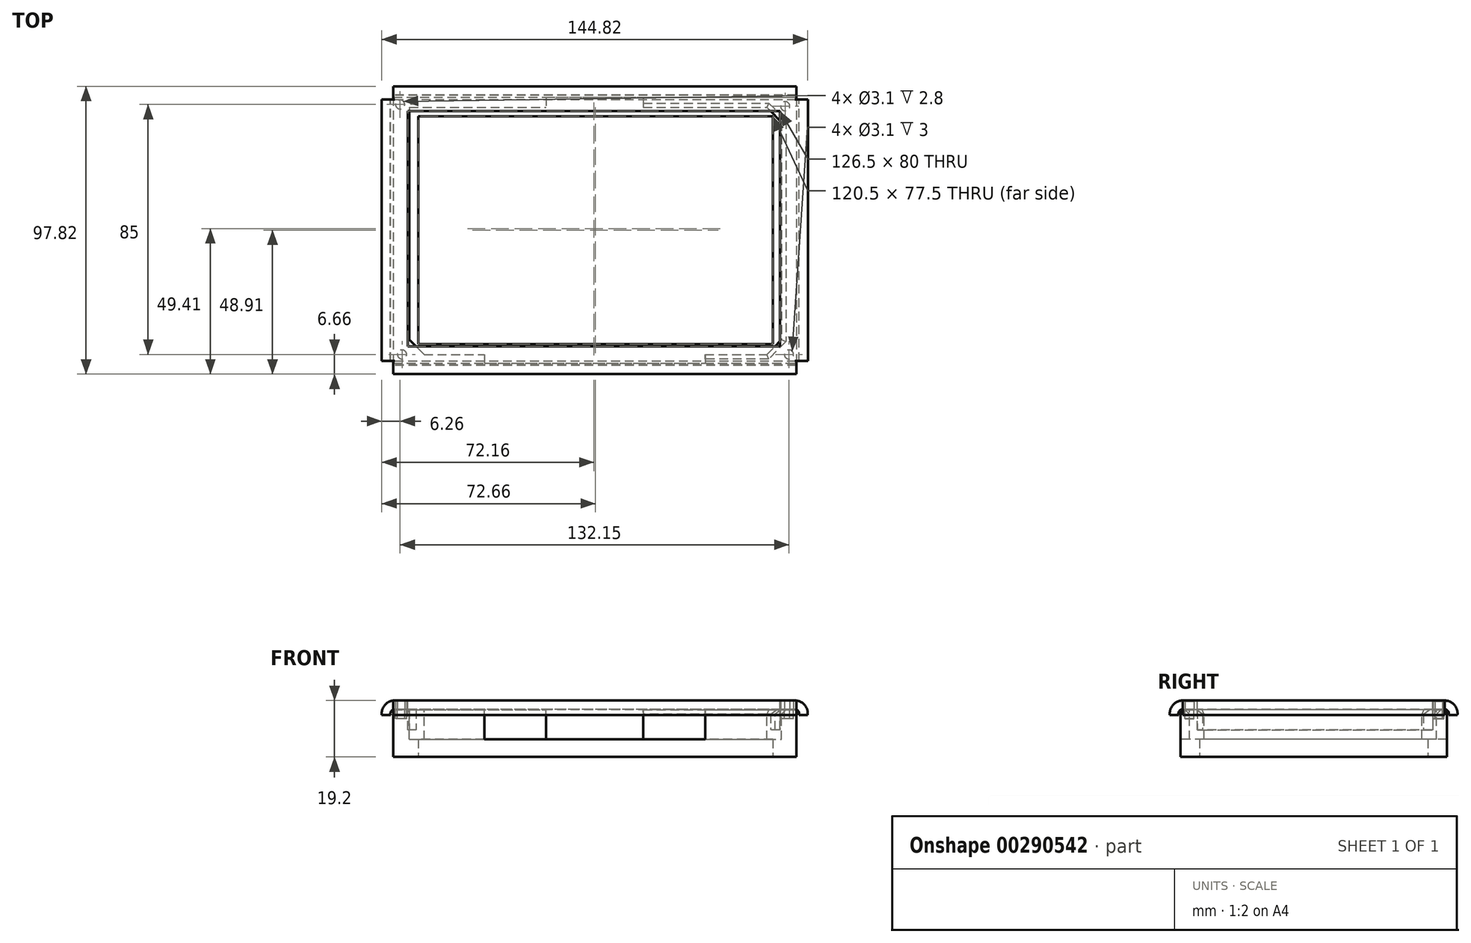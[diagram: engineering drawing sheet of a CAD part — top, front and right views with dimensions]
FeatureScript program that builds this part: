
annotation { "Feature Type Name" : "Feature", "Feature Type Description" : "" }
export const myFeature = defineFeature(function(context is Context, id is Id, definition is map)
    precondition{}
    {
        {
            var Q0;
            Q0=qCreatedBy(makeId("Top.planeOp"),FACE);
            var sketch = newSketch(context, id + "F0", { "sketchPlane" : qUnion([Q0])});
            skLineSegment(sketch, "E0.top", {"start": v(-68.5, -45.25) * mm, "end": v(68.5, -45.25) * mm});
            skLineSegment(sketch, "E0.left", {"start": v(-68.5, 45.25) * mm, "end": v(-68.5, -45.25) * mm});
            skLineSegment(sketch, "E0.right", {"start": v(68.5, 45.25) * mm, "end": v(68.5, -45.25) * mm});
            skLineSegment(sketch, "E1.top", {"start": v(-60, -38.75) * mm, "end": v(60.5, -38.75) * mm});
            skLineSegment(sketch, "E1.left", {"start": v(-60, 38.75) * mm, "end": v(-60, -38.75) * mm});
            skLineSegment(sketch, "E1.right", {"start": v(60.5, 38.75) * mm, "end": v(60.5, -38.75) * mm});
            skLineSegment(sketch, "E2", {"start": v(-68.5, 45.25) * mm, "end": v(68.5, 45.25) * mm});
            skLineSegment(sketch, "E3", {"start": v(60.5, 38.75) * mm, "end": v(-60, 38.75) * mm});
            skSolve(sketch);
        }
        {
            var Q0;
            Q0=makeQuery(id+"F0.imprint","IMPRINT",FACE,{"disambiguationData":[TD([[makeQuery(id+"F0.imprint","IMPRINT",EDGE,{"derivedFrom":sQuery(id+"F0.wireOp",EDGE,"E0.top")}),1.0]])]});
            extrude(context, id + "F1", {"entities" : qUnion([Q0]), "depth" : 16 * mm});
        }
        {
            var Q0;
            Q0=makeQuery(id+"F1.opExtrude","CAP_VERTEX",VERTEX,{"disambiguationData":[OSD([sQuery(id+"F0.wireOp",EDGE,"E0.left"),sQuery(id+"F0.wireOp",EDGE,"E2")])],"isStart":false});
            var Q1;
            Q1=makeQuery(id+"F1.opExtrude","CAP_VERTEX",VERTEX,{"disambiguationData":[OSD([sQuery(id+"F0.wireOp",EDGE,"E1.left"),sQuery(id+"F0.wireOp",EDGE,"E3")])],"isStart":false});
            var Q2;
            Q2=makeQuery(id+"F1.opExtrude","CAP_VERTEX",VERTEX,{"disambiguationData":[OSD([sQuery(id+"F0.wireOp",EDGE,"E1.top"),sQuery(id+"F0.wireOp",EDGE,"E1.left")])],"isStart":false});
            cPlane(context, id + "F2", {"entities" : qUnion([Q0, Q1, Q2]), "cplaneType" : CPlaneType.THREE_POINT, "offset" : 25 * mm, "width" : 150 * mm, "height" : 150 * mm});
        }
        {
            var Q0;
            Q0=qCreatedBy(id+"F2.planeOp",FACE);
            var sketch = newSketch(context, id + "F3", { "sketchPlane" : qUnion([Q0])});
            skLineSegment(sketch, "E4.bottom", {"start": v(-16.5, 80.88) * mm, "end": v(16.5, 80.88) * mm});
            skLineSegment(sketch, "E4.top", {"start": v(-16.5, 28.75) * mm, "end": v(16.5, 28.75) * mm});
            skLineSegment(sketch, "E4.left", {"start": v(-16.5, 80.88) * mm, "end": v(-16.5, 28.75) * mm});
            skLineSegment(sketch, "E4.right", {"start": v(16.5, 80.88) * mm, "end": v(16.5, 28.75) * mm});
            skLineSegment(sketch, "E5.bottom", {"start": v(-63, 41.75) * mm, "end": v(58.5, 41.75) * mm});
            skLineSegment(sketch, "E5.top", {"start": v(-58, -42.25) * mm, "end": v(58.5, -42.25) * mm});
            skLineSegment(sketch, "E5.left", {"start": v(-63, 41.75) * mm, "end": v(-63, -37.25) * mm});
            skLineSegment(sketch, "E6.bottom", {"start": v(37.5, -28.75) * mm, "end": v(-37.5, -28.75) * mm});
            skLineSegment(sketch, "E6.top", {"start": v(37.5, -48.75) * mm, "end": v(-37.5, -48.75) * mm});
            skLineSegment(sketch, "E6.left", {"start": v(37.5, -28.75) * mm, "end": v(37.5, -48.75) * mm});
            skLineSegment(sketch, "E6.right", {"start": v(-37.5, -28.75) * mm, "end": v(-37.5, -48.75) * mm});
            skLineSegment(sketch, "E7", {"start": v(-63, -37.25) * mm, "end": v(-58, -42.25) * mm});
            skLineSegment(sketch, "E8", {"start": v(58.5, -42.25) * mm, "end": v(63.5, -37.25) * mm});
            skLineSegment(sketch, "E9", {"start": v(58.5, 41.75) * mm, "end": v(63.5, 36.75) * mm});
            skLineSegment(sketch, "E10", {"start": v(63.5, 36.75) * mm, "end": v(63.5, -37.25) * mm});
            skSolve(sketch);
        }
        {
            var Q0;
            {var subQ0=sQuery(id+"F3.wireOp",EDGE,"E4.bottom");Q0=makeQuery(id+"F3.imprint","IMPRINT",FACE,{"disambiguationData":[TD([[makeQuery(id+"F3.imprint","IMPRINT",EDGE,{"derivedFrom":subQ0}),-1.0]])]});}
            var Q1;
            {var subQ0=sQuery(id+"F3.wireOp",EDGE,"E4.top");Q1=makeQuery(id+"F3.imprint","IMPRINT",FACE,{"disambiguationData":[TD([[makeQuery(id+"F3.imprint","IMPRINT",EDGE,{"derivedFrom":subQ0}),1.0]])]});}
            var Q2;
            {var subQ10=sQuery(id+"F3.wireOp",EDGE,"E4.top");Q2=makeQuery(id+"F3.imprint","IMPRINT",FACE,{"disambiguationData":[TD([[makeQuery(id+"F3.imprint","IMPRINT",EDGE,{"derivedFrom":subQ10}),-1.0]])]});}
            var Q3;
            {var subQ5=sQuery(id+"F3.wireOp",EDGE,"E6.bottom");Q3=makeQuery(id+"F3.imprint","IMPRINT",FACE,{"disambiguationData":[TD([[makeQuery(id+"F3.imprint","IMPRINT",EDGE,{"derivedFrom":subQ5}),1.0]])]});}
            var Q4;
            {var subQ5=sQuery(id+"F3.wireOp",EDGE,"E6.top");Q4=makeQuery(id+"F3.imprint","IMPRINT",FACE,{"disambiguationData":[TD([[makeQuery(id+"F3.imprint","IMPRINT",EDGE,{"derivedFrom":subQ5}),-1.0]])]});}
            extrude(context, id + "F4", {"entities" : qUnion([Q0, Q1, Q2, Q3, Q4]), "operationType" : NewBodyOperationType.REMOVE, "oppositeDirection" : true, "depth" : 10 * mm});
        }
        {
            var Q0;
            Q0=makeQuery(id+"F4.boolean.opBoolean","COPY",EDGE,{"derivedFrom":makeQuery(id+"F4.opExtrude","CAP_EDGE",EDGE,{"disambiguationData":[OSD([sQuery(id+"F3.wireOp",EDGE,"E5.left")])],"isStart":true})});
            var Q1;
            {var subQ0=sQuery(id+"F3.wireOp",EDGE,"E5.bottom");Q1=makeQuery(id+"F4.boolean.opBoolean","COPY",EDGE,{"derivedFrom":makeQuery(id+"F4.opExtrude","CAP_EDGE",EDGE,{"disambiguationData":[OSD([subQ0]),TDD([makeQuery(id+"F3.imprint","IMPRINT",EDGE,{"disambiguationData":[TD([[makeQuery(id+"F3.imprint","INTERSECT",VERTEX,{"derivedFrom":[subQ0,sQuery(id+"F3.wireOp",EDGE,"E5.left")]}),-1.0]])],"derivedFrom":subQ0})])],"isStart":true})});}
            var Q2;
            {var subQ0=sQuery(id+"F3.wireOp",EDGE,"E5.bottom");Q2=makeQuery(id+"F4.boolean.opBoolean","COPY",EDGE,{"derivedFrom":makeQuery(id+"F4.opExtrude","CAP_EDGE",EDGE,{"disambiguationData":[OSD([subQ0]),TDD([makeQuery(id+"F3.imprint","IMPRINT",EDGE,{"disambiguationData":[TD([[makeQuery(id+"F3.imprint","INTERSECT",VERTEX,{"derivedFrom":[subQ0,sQuery(id+"F3.wireOp",EDGE,"E5.right")]}),1.0]])],"derivedFrom":subQ0})])],"isStart":true})});}
            var Q3;
            Q3=makeQuery(id+"F4.boolean.opBoolean","COPY",EDGE,{"derivedFrom":makeQuery(id+"F4.opExtrude","CAP_EDGE",EDGE,{"disambiguationData":[OSD([sQuery(id+"F3.wireOp",EDGE,"E5.right")])],"isStart":true})});
            var Q4;
            {var subQ0=sQuery(id+"F3.wireOp",EDGE,"E5.top");Q4=makeQuery(id+"F4.boolean.opBoolean","COPY",EDGE,{"derivedFrom":makeQuery(id+"F4.opExtrude","CAP_EDGE",EDGE,{"disambiguationData":[OSD([subQ0]),TDD([makeQuery(id+"F3.imprint","IMPRINT",EDGE,{"disambiguationData":[TD([[makeQuery(id+"F3.imprint","INTERSECT",VERTEX,{"derivedFrom":[subQ0,sQuery(id+"F3.wireOp",EDGE,"E5.right")]}),1.0]])],"derivedFrom":subQ0})])],"isStart":true})});}
            var Q5;
            {var subQ0=sQuery(id+"F3.wireOp",EDGE,"E5.top");Q5=makeQuery(id+"F4.boolean.opBoolean","COPY",EDGE,{"derivedFrom":makeQuery(id+"F4.opExtrude","CAP_EDGE",EDGE,{"disambiguationData":[OSD([subQ0]),TDD([makeQuery(id+"F3.imprint","IMPRINT",EDGE,{"disambiguationData":[TD([[makeQuery(id+"F3.imprint","INTERSECT",VERTEX,{"derivedFrom":[subQ0,sQuery(id+"F3.wireOp",EDGE,"E5.left")]}),-1.0]])],"derivedFrom":subQ0})])],"isStart":true})});}
            var Q6;
            Q6=makeQuery(id+"F4.boolean.opBoolean","COPY",EDGE,{"derivedFrom":makeQuery(id+"F4.opExtrude","CAP_EDGE",EDGE,{"disambiguationData":[OSD([sQuery(id+"F3.wireOp",EDGE,"E9")])],"isStart":true})});
            var Q7;
            Q7=makeQuery(id+"F4.boolean.opBoolean","COPY",EDGE,{"derivedFrom":makeQuery(id+"F4.opExtrude","CAP_EDGE",EDGE,{"disambiguationData":[OSD([sQuery(id+"F3.wireOp",EDGE,"E10")])],"isStart":true})});
            var Q8;
            Q8=makeQuery(id+"F4.boolean.opBoolean","COPY",EDGE,{"derivedFrom":makeQuery(id+"F4.opExtrude","CAP_EDGE",EDGE,{"disambiguationData":[OSD([sQuery(id+"F3.wireOp",EDGE,"E8")])],"isStart":true})});
            var Q9;
            Q9=makeQuery(id+"F4.boolean.opBoolean","COPY",EDGE,{"derivedFrom":makeQuery(id+"F4.opExtrude","CAP_EDGE",EDGE,{"disambiguationData":[OSD([sQuery(id+"F3.wireOp",EDGE,"E7")])],"isStart":true})});
            chamfer(context, id + "F5", {"entities" : qUnion([Q0, Q1, Q2, Q3, Q4, Q5, Q6, Q7, Q8, Q9]), "width" : 1.5 * mm, "tangentPropagation" : true});
        }
        {
            var Q0;
            {var subQ1=sQuery(id+"F0.wireOp",EDGE,"E2");var subQ2=sQuery(id+"F0.wireOp",EDGE,"E0.left");var subQ5=sQuery(id+"F0.wireOp",EDGE,"E0.top");Q0=makeQuery(id+"F4.boolean.opBoolean","SPLIT",FACE,{"disambiguationData":[TD([makeQuery(id+"F1.opExtrude","SWEPT_FACE",FACE,{"disambiguationData":[OSD([subQ2])]})])],"derivedFrom":makeQuery(id+"F1.opExtrude","CAP_FACE",FACE,{"disambiguationData":[OSD([subQ5,subQ2,sQuery(id+"F0.wireOp",EDGE,"E0.right"),sQuery(id+"F0.wireOp",EDGE,"E1.top"),sQuery(id+"F0.wireOp",EDGE,"E1.left"),sQuery(id+"F0.wireOp",EDGE,"E1.right"),subQ1,sQuery(id+"F0.wireOp",EDGE,"E3")])],"isStart":false})});}
            var Q1;
            {var subQ1=sQuery(id+"F0.wireOp",EDGE,"E2");var subQ2=sQuery(id+"F0.wireOp",EDGE,"E0.left");var subQ5=sQuery(id+"F0.wireOp",EDGE,"E0.top");Q1=makeQuery(id+"F4.boolean.opBoolean","SPLIT",FACE,{"disambiguationData":[TD([makeQuery(id+"F1.opExtrude","SWEPT_FACE",FACE,{"disambiguationData":[OSD([subQ2])]})])],"derivedFrom":makeQuery(id+"F1.opExtrude","CAP_FACE",FACE,{"disambiguationData":[OSD([subQ5,subQ2,sQuery(id+"F0.wireOp",EDGE,"E0.right"),sQuery(id+"F0.wireOp",EDGE,"E1.top"),sQuery(id+"F0.wireOp",EDGE,"E1.left"),sQuery(id+"F0.wireOp",EDGE,"E1.right"),subQ1,sQuery(id+"F0.wireOp",EDGE,"E3")])],"isStart":false})});}
            var Q2;
            {var subQ1=sQuery(id+"F0.wireOp",EDGE,"E2");var subQ2=sQuery(id+"F0.wireOp",EDGE,"E0.left");var subQ5=sQuery(id+"F0.wireOp",EDGE,"E0.top");Q2=makeQuery(id+"F4.boolean.opBoolean","SPLIT",FACE,{"disambiguationData":[TD([makeQuery(id+"F1.opExtrude","SWEPT_FACE",FACE,{"disambiguationData":[OSD([subQ2])]})])],"derivedFrom":makeQuery(id+"F1.opExtrude","CAP_FACE",FACE,{"disambiguationData":[OSD([subQ5,subQ2,sQuery(id+"F0.wireOp",EDGE,"E0.right"),sQuery(id+"F0.wireOp",EDGE,"E1.top"),sQuery(id+"F0.wireOp",EDGE,"E1.left"),sQuery(id+"F0.wireOp",EDGE,"E1.right"),subQ1,sQuery(id+"F0.wireOp",EDGE,"E3")])],"isStart":false})});}
            var sketch = newSketch(context, id + "F6", { "sketchPlane" : qUnion([Q0, Q1, Q2])});
            skCircle(sketch, "E11", {"center": v(-66.15, 42.75) * mm, "radius": 1.55 * mm});
            skCircle(sketch, "E12", {"center": v(-65.5, -42.25) * mm, "radius": 1.55 * mm});
            skCircle(sketch, "E13", {"center": v(66, -42.25) * mm, "radius": 1.55 * mm});
            skCircle(sketch, "E14", {"center": v(64.73, 42.15) * mm, "radius": 1.55 * mm});
            skSolve(sketch);
        }
        {
            var Q0;
            Q0=makeQuery(id+"F6.imprint","IMPRINT",FACE,{"disambiguationData":[TD([[makeQuery(id+"F6.imprint","IMPRINT",EDGE,{"derivedFrom":sQuery(id+"F6.wireOp",EDGE,"E11")}),1.0]])]});
            var Q1;
            Q1=makeQuery(id+"F6.imprint","IMPRINT",FACE,{"disambiguationData":[TD([[makeQuery(id+"F6.imprint","IMPRINT",EDGE,{"derivedFrom":sQuery(id+"F6.wireOp",EDGE,"E12")}),1.0]])]});
            var Q2;
            Q2=makeQuery(id+"F6.imprint","IMPRINT",FACE,{"disambiguationData":[TD([[makeQuery(id+"F6.imprint","IMPRINT",EDGE,{"derivedFrom":sQuery(id+"F6.wireOp",EDGE,"E13")}),1.0]])]});
            var Q3;
            Q3=makeQuery(id+"F6.imprint","IMPRINT",FACE,{"disambiguationData":[TD([[makeQuery(id+"F6.imprint","IMPRINT",EDGE,{"derivedFrom":sQuery(id+"F6.wireOp",EDGE,"E14")}),1.0]])]});
            extrude(context, id + "F7", {"entities" : qUnion([Q0, Q1, Q2, Q3]), "operationType" : NewBodyOperationType.REMOVE, "oppositeDirection" : true, "depth" : 3 * mm});
        }
        {
            var Q0;
            Q0=makeQuery(id+"F6.imprint","IMPRINT",FACE,{"disambiguationData":[TD([[makeQuery(id+"F6.imprint","IMPRINT",EDGE,{"derivedFrom":sQuery(id+"F6.wireOp",EDGE,"E11")}),1.0]])]});
            var Q1;
            Q1=makeQuery(id+"F6.imprint","IMPRINT",FACE,{"disambiguationData":[TD([[makeQuery(id+"F6.imprint","IMPRINT",EDGE,{"derivedFrom":sQuery(id+"F6.wireOp",EDGE,"E12")}),1.0]])]});
            var Q2;
            Q2=makeQuery(id+"F6.imprint","IMPRINT",FACE,{"disambiguationData":[TD([[makeQuery(id+"F6.imprint","IMPRINT",EDGE,{"derivedFrom":sQuery(id+"F6.wireOp",EDGE,"E13")}),1.0]])]});
            var Q3;
            Q3=makeQuery(id+"F6.imprint","IMPRINT",FACE,{"disambiguationData":[TD([[makeQuery(id+"F6.imprint","IMPRINT",EDGE,{"derivedFrom":sQuery(id+"F6.wireOp",EDGE,"E14")}),1.0]])]});
            extrude(context, id + "F8", {"entities" : qUnion([Q0, Q1, Q2, Q3]), "oppositeDirection" : true, "depth" : 3 * mm});
        }
        {
            var Q0;
            Q0=qCreatedBy(makeId("Front.planeOp"),FACE);
            var sketch = newSketch(context, id + "F9", { "sketchPlane" : qUnion([Q0])});
            skLineSegment(sketch, "E15.bottom", {"start": v(-68, 19.2) * mm, "end": v(68, 19.2) * mm});
            skLineSegment(sketch, "E15.top", {"start": v(-68, 16.2) * mm, "end": v(68, 16.2) * mm});
            skLineSegment(sketch, "E15.left", {"start": v(-68, 19.2) * mm, "end": v(-68, 16.2) * mm});
            skLineSegment(sketch, "E15.right", {"start": v(68, 19.2) * mm, "end": v(68, 16.2) * mm});
            skArc(sketch, "E16", {"start": v(69.38, 14.23) * mm, "mid": v(69.2, 15.58) * mm, "end": v(68, 16.2) * mm});
            skArc(sketch, "E17", {"start": v(72.38, 14.23) * mm, "mid": v(71.31, 17.7) * mm, "end": v(68, 19.2) * mm});
            skLineSegment(sketch, "E18", {"start": v(69.38, 14.23) * mm, "end": v(72.38, 14.23) * mm});
            skArc(sketch, "E19.MirrorCS", {"start": v(-69.38, 14.23) * mm, "mid": v(-69.2, 15.58) * mm, "end": v(-68, 16.2) * mm});
            skArc(sketch, "E20.MirrorCS", {"start": v(-72.38, 14.23) * mm, "mid": v(-71.31, 17.7) * mm, "end": v(-68, 19.2) * mm});
            skLineSegment(sketch, "E21.MirrorCS", {"start": v(-69.38, 14.23) * mm, "end": v(-72.38, 14.23) * mm});
            skSolve(sketch);
        }
        {
            var Q0;
            Q0 = qSketchRegion(id + "F9", true);
            extrude(context, id + "F10", {"entities" : qUnion([Q0]), "endBound" : BoundingType.SYMMETRIC, "depth" : 89 * mm});
        }
        {
            var Q0;
            Q0=qCreatedBy(makeId("Right.planeOp"),FACE);
            var sketch = newSketch(context, id + "F11", { "sketchPlane" : qUnion([Q0])});
            skLineSegment(sketch, "E22.right", {"start": v(44.5, 19.2) * mm, "end": v(44.5, 16.2) * mm});
            skArc(sketch, "E23", {"start": v(45.88, 14.23) * mm, "mid": v(45.72, 15.59) * mm, "end": v(44.5, 16.2) * mm});
            skArc(sketch, "E24", {"start": v(48.88, 14.23) * mm, "mid": v(47.81, 17.7) * mm, "end": v(44.5, 19.2) * mm});
            skLineSegment(sketch, "E25", {"start": v(45.88, 14.23) * mm, "end": v(48.88, 14.23) * mm});
            skArc(sketch, "E26.MirrorCS", {"start": v(-48.88, 14.23) * mm, "mid": v(-47.81, 17.7) * mm, "end": v(-44.5, 19.2) * mm});
            skArc(sketch, "E27.MirrorCS", {"start": v(-45.88, 14.23) * mm, "mid": v(-45.72, 15.59) * mm, "end": v(-44.5, 16.2) * mm});
            skLineSegment(sketch, "E28.MirrorCS", {"start": v(-45.88, 14.23) * mm, "end": v(-48.88, 14.23) * mm});
            skLineSegment(sketch, "E29.MirrorCS", {"start": v(-44.5, 19.2) * mm, "end": v(-44.5, 16.2) * mm});
            skSolve(sketch);
        }
        {
            var Q0;
            Q0 = qSketchRegion(id + "F11", true);
            extrude(context, id + "F12", {"entities" : qUnion([Q0]), "operationType" : NewBodyOperationType.ADD, "endBound" : BoundingType.SYMMETRIC, "depth" : 137 * mm});
        }
        {
            var Q0;
            Q0=makeQuery(id+"F10.opExtrude","SWEPT_FACE",FACE,{"disambiguationData":[OSD([sQuery(id+"F9.wireOp",EDGE,"E15.bottom")])]});
            var sketch = newSketch(context, id + "F13", { "sketchPlane" : qUnion([Q0])});
            skLineSegment(sketch, "E30.bottom", {"start": v(63, 40.5) * mm, "end": v(-63.5, 40.5) * mm});
            skLineSegment(sketch, "E30.top", {"start": v(63, -39.5) * mm, "end": v(-63.5, -39.5) * mm});
            skLineSegment(sketch, "E30.left", {"start": v(63, 40.5) * mm, "end": v(63, -39.5) * mm});
            skLineSegment(sketch, "E30.right", {"start": v(-63.5, 40.5) * mm, "end": v(-63.5, -39.5) * mm});
            skSolve(sketch);
        }
        {
            var Q0;
            Q0=makeQuery(id+"F13.imprint","IMPRINT",FACE,{"disambiguationData":[TD([[makeQuery(id+"F13.imprint","IMPRINT",EDGE,{"derivedFrom":sQuery(id+"F13.wireOp",EDGE,"E30.bottom")}),1.0]])]});
            extrude(context, id + "F14", {"entities" : qUnion([Q0]), "operationType" : NewBodyOperationType.REMOVE, "oppositeDirection" : true, "depth" : 10 * mm});
        }
        {
            var Q0;
            Q0 = qSketchRegion(id + "F6", true);
            extrude(context, id + "F15", {"entities" : qUnion([Q0]), "operationType" : NewBodyOperationType.REMOVE, "depth" : 3 * mm});
        }
    });
